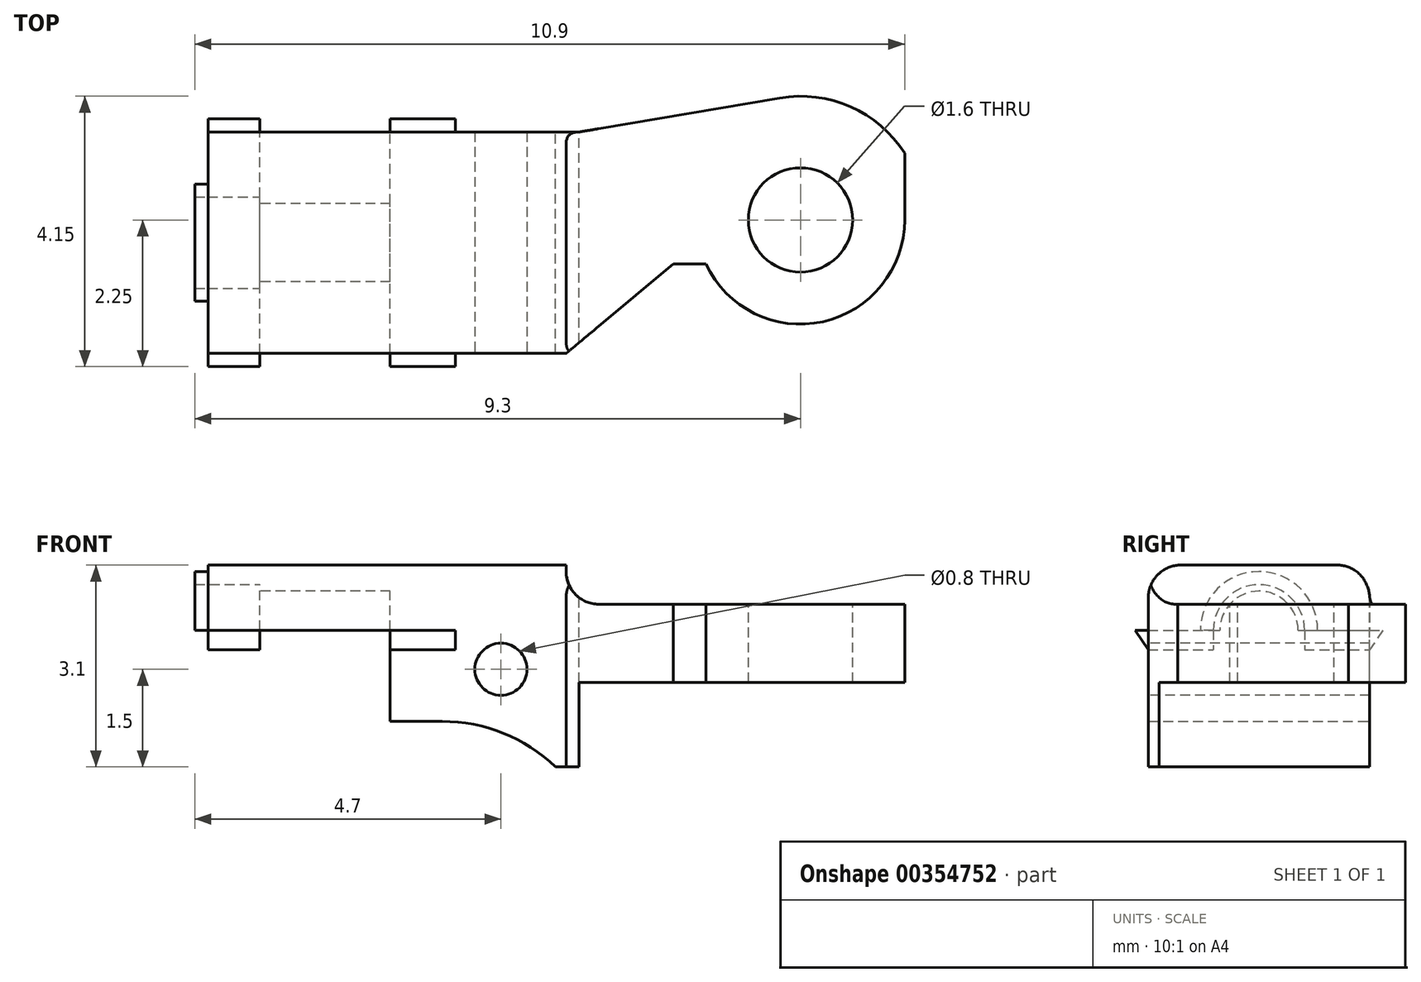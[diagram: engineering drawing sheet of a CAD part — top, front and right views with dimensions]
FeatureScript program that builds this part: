
annotation { "Feature Type Name" : "Feature", "Feature Type Description" : "" }
export const myFeature = defineFeature(function(context is Context, id is Id, definition is map)
    precondition{}
    {
        {
            var Q0;
            Q0=qCreatedBy(makeId("Front.planeOp"),FACE);
            var sketch = newSketch(context, id + "F0", { "sketchPlane" : qUnion([Q0])});
            skLineSegment(sketch, "E0", {"start": v(0, 0) * mm, "end": v(0, 2.4) * mm});
            skLineSegment(sketch, "E1", {"start": v(0, 2.4) * mm, "end": v(4.7, 2.4) * mm});
            skLineSegment(sketch, "E2", {"start": v(4.7, 2.4) * mm, "end": v(4.7, 2.4) * mm});
            skLineSegment(sketch, "E3", {"start": v(4.7, 1.8) * mm, "end": v(4.7, 2.4) * mm});
            skLineSegment(sketch, "E4", {"start": v(4.7, 1.8) * mm, "end": v(9.9, 1.8) * mm});
            skLineSegment(sketch, "E5", {"start": v(9.9, 1.8) * mm, "end": v(9.9, 0.6) * mm});
            skLineSegment(sketch, "E6", {"start": v(9.9, 0.6) * mm, "end": v(4.9, 0.6) * mm});
            skLineSegment(sketch, "E7", {"start": v(4.9, 0.6) * mm, "end": v(4.9, -0.7) * mm});
            skLineSegment(sketch, "E8", {"start": v(2.8, 0) * mm, "end": v(0, 0) * mm});
            skArc(sketch, "E9", {"start": v(4.53, -0.7) * mm, "mid": v(3.74, -0.18) * mm, "end": v(2.8, 0) * mm});
            skLineSegment(sketch, "E10", {"start": v(4.53, -0.7) * mm, "end": v(4.9, -0.7) * mm});
            skPoint(sketch, "E11.orphan", {"position": v(4.9, 0) * mm});
            skSolve(sketch);
        }
        {
            var Q0;
            Q0 = qSketchRegion(id + "F0", true);
            extrude(context, id + "F1", {"entities" : qUnion([Q0]), "endBound" : BoundingType.SYMMETRIC, "depth" : 3.4 * mm});
        }
        {
            var Q0;
            Q0=makeQuery(id+"F1.opExtrude","SWEPT_FACE",FACE,{"disambiguationData":[OSD([sQuery(id+"F0.wireOp",EDGE,"E4")])]});
            var sketch = newSketch(context, id + "F2", { "sketchPlane" : qUnion([Q0])});
            skCircle(sketch, "E12", {"center": v(8.3, 0.35) * mm, "radius": 0.8 * mm});
            skArc(sketch, "E13", {"start": v(9.9, 0.35) * mm, "mid": v(8.65, -1.21) * mm, "end": v(6.85, -0.33) * mm});
            skLineSegment(sketch, "E14", {"start": v(8.3, 0.35) * mm, "end": v(6.85, -0.33) * mm, "construction": true});
            skLineSegment(sketch, "E15", {"start": v(4.7, -1.7) * mm, "end": v(6.35, -0.33) * mm});
            skLineSegment(sketch, "E16", {"start": v(6.35, -0.33) * mm, "end": v(6.85, -0.33) * mm});
            skLineSegment(sketch, "E17", {"start": v(9.9, 1.7) * mm, "end": v(9.9, 1.37) * mm});
            skLineSegment(sketch, "E18", {"start": v(9.9, -1.7) * mm, "end": v(4.7, -1.7) * mm});
            skPoint(sketch, "E19.orphan", {"position": v(6.85, -0.33) * mm});
            skLineSegment(sketch, "E20", {"start": v(9.9, 1.7) * mm, "end": v(9.64, 1.7) * mm});
            skPoint(sketch, "E21.orphan", {"position": v(9.9, 0.35) * mm});
            skArc(sketch, "E22", {"start": v(9.9, 1.37) * mm, "mid": v(9.78, 1.54) * mm, "end": v(9.64, 1.7) * mm});
            skLineSegment(sketch, "E23.trimOffspring", {"start": v(9.9, 0.35) * mm, "end": v(9.9, -1.7) * mm});
            skSolve(sketch);
        }
        {
            var Q0;
            Q0 = qSketchRegion(id + "F2", true);
            extrude(context, id + "F3", {"entities" : qUnion([Q0]), "operationType" : NewBodyOperationType.REMOVE, "endBound" : BoundingType.THROUGH_ALL, "oppositeDirection" : true, "depth" : 25 * mm});
        }
        {
            var Q0;
            Q0=makeQuery(id+"F1.opExtrude","SWEPT_FACE",FACE,{"disambiguationData":[OSD([sQuery(id+"F0.wireOp",EDGE,"E4")])]});
            var sketch = newSketch(context, id + "F4", { "sketchPlane" : qUnion([Q0])});
            skArc(sketch, "E24", {"start": v(9.64, 1.7) * mm, "mid": v(8.87, 2.16) * mm, "end": v(7.98, 2.22) * mm});
            skLineSegment(sketch, "E25", {"start": v(4.9, 1.7) * mm, "end": v(7.98, 2.22) * mm});
            skLineSegment(sketch, "E26", {"start": v(4.9, 1.7) * mm, "end": v(9.64, 1.7) * mm});
            skSolve(sketch);
        }
        {
            var Q0;
            Q0=makeQuery(id+"F4.imprint","IMPRINT",FACE,{"disambiguationData":[TD([[makeQuery(id+"F4.imprint","IMPRINT",EDGE,{"derivedFrom":sQuery(id+"F4.wireOp",EDGE,"E24")}),1.0]])]});
            var Q1;
            Q1=makeQuery(id+"F1.opExtrude","SWEPT_FACE",FACE,{"disambiguationData":[OSD([sQuery(id+"F0.wireOp",EDGE,"E6")])]});
            extrude(context, id + "F5", {"entities" : qUnion([Q0]), "operationType" : NewBodyOperationType.ADD, "endBound" : BoundingType.UP_TO_SURFACE, "oppositeDirection" : true, "endBoundEntityFace" : qUnion([Q1]), "depth" : 25 * mm});
        }
        {
            var Q0;
            Q0=makeQuery(id+"F1.opExtrude","SWEPT_FACE",FACE,{"disambiguationData":[OSD([sQuery(id+"F0.wireOp",EDGE,"E0")])]});
            var sketch = newSketch(context, id + "F6", { "sketchPlane" : qUnion([Q0])});
            skLineSegment(sketch, "E27.bottom", {"start": v(1.7, 0) * mm, "end": v(-1.7, 0) * mm});
            skLineSegment(sketch, "E27.top", {"start": v(1.7, 1.4) * mm, "end": v(0.6, 1.4) * mm});
            skLineSegment(sketch, "E27.left", {"start": v(1.7, 0) * mm, "end": v(1.7, 1.4) * mm});
            skLineSegment(sketch, "E27.right", {"start": v(-1.7, 0) * mm, "end": v(-1.7, 1.4) * mm});
            skArc(sketch, "E28", {"start": v(0.6, 1.4) * mm, "mid": v(0, 2) * mm, "end": v(-0.6, 1.4) * mm});
            skLineSegment(sketch, "E29.trimOffspring", {"start": v(-0.6, 1.4) * mm, "end": v(-1.7, 1.4) * mm});
            skSolve(sketch);
        }
        {
            var Q0;
            Q0 = qSketchRegion(id + "F6", true);
            extrude(context, id + "F7", {"entities" : qUnion([Q0]), "operationType" : NewBodyOperationType.REMOVE, "oppositeDirection" : true, "depth" : 2 * mm});
        }
        {
            var Q0;
            Q0=makeQuery(id+"F1.opExtrude","SWEPT_FACE",FACE,{"disambiguationData":[OSD([sQuery(id+"F0.wireOp",EDGE,"E0")])]});
            var sketch = newSketch(context, id + "F8", { "sketchPlane" : qUnion([Q0])});
            skArc(sketch, "E30", {"start": v(0.7, 1.4) * mm, "mid": v(0, 2.1) * mm, "end": v(-0.7, 1.4) * mm});
            skLineSegment(sketch, "E31", {"start": v(-0.7, 1.1) * mm, "end": v(-1.7, 1.1) * mm});
            skLineSegment(sketch, "E32", {"start": v(1.7, 2.4) * mm, "end": v(1.7, 1.1) * mm});
            skLineSegment(sketch, "E33", {"start": v(1.7, 1.1) * mm, "end": v(0.7, 1.1) * mm});
            skLineSegment(sketch, "E34", {"start": v(0.7, 1.4) * mm, "end": v(0.7, 1.1) * mm});
            skLineSegment(sketch, "E35", {"start": v(-0.7, 1.4) * mm, "end": v(-0.7, 1.1) * mm});
            skLineSegment(sketch, "E36", {"start": v(1.7, 2.4) * mm, "end": v(-1.7, 2.4) * mm});
            skLineSegment(sketch, "E37", {"start": v(-1.7, 2.4) * mm, "end": v(-1.7, 1.1) * mm});
            skSolve(sketch);
        }
        {
            var Q0;
            Q0 = qSketchRegion(id + "F8", true);
            extrude(context, id + "F9", {"entities" : qUnion([Q0]), "operationType" : NewBodyOperationType.ADD, "depth" : 0.8 * mm});
        }
        {
            var Q0;
            Q0=makeQuery(id+"F9.opExtrude","CAP_FACE",FACE,{"disambiguationData":[OSD([sQuery(id+"F8.wireOp",EDGE,"E30"),sQuery(id+"F8.wireOp",EDGE,"33daba41-ab30-421a-8f09-6baf427ecfd6"),sQuery(id+"F8.wireOp",EDGE,"E31"),sQuery(id+"F8.wireOp",EDGE,"E32"),sQuery(id+"F8.wireOp",EDGE,"E33"),sQuery(id+"F8.wireOp",EDGE,"E34"),sQuery(id+"F8.wireOp",EDGE,"E35"),sQuery(id+"F8.wireOp",EDGE,"E36"),sQuery(id+"F8.wireOp",EDGE,"E37"),sQuery(id+"F8.wireOp",EDGE,"b7cedbdc-8d8d-4e8a-a9b7-a7e40b9fc0be.trimOffspring")])],"isStart":false});
            var sketch = newSketch(context, id + "F10", { "sketchPlane" : qUnion([Q0])});
            skArc(sketch, "E38", {"start": v(0.7, 1.4) * mm, "mid": v(0, 2.1) * mm, "end": v(-0.7, 1.4) * mm});
            skArc(sketch, "E39", {"start": v(0.9, 1.4) * mm, "mid": v(0, 2.3) * mm, "end": v(-0.9, 1.4) * mm});
            skLineSegment(sketch, "E40", {"start": v(0.7, 1.4) * mm, "end": v(0.9, 1.4) * mm});
            skLineSegment(sketch, "E41", {"start": v(-0.7, 1.4) * mm, "end": v(-0.9, 1.4) * mm});
            skSolve(sketch);
        }
        {
            var Q0;
            Q0 = qSketchRegion(id + "F10", true);
            extrude(context, id + "F11", {"entities" : qUnion([Q0]), "operationType" : NewBodyOperationType.ADD, "depth" : 0.2 * mm});
        }
        {
            var Q0;
            Q0=makeQuery(id+"F9.boolean.opBoolean","MERGE",FACE,{"derivedFrom":[makeQuery(id+"F1.opExtrude","CAP_FACE",FACE,{"disambiguationData":[OSD([sQuery(id+"F0.wireOp",EDGE,"E0"),sQuery(id+"F0.wireOp",EDGE,"E1"),sQuery(id+"F0.wireOp",EDGE,"E3"),sQuery(id+"F0.wireOp",EDGE,"E4"),sQuery(id+"F0.wireOp",EDGE,"E5"),sQuery(id+"F0.wireOp",EDGE,"E6"),sQuery(id+"F0.wireOp",EDGE,"E7"),sQuery(id+"F0.wireOp",EDGE,"E8"),sQuery(id+"F0.wireOp",EDGE,"E9"),sQuery(id+"F0.wireOp",EDGE,"E10")])],"isStart":false}),makeQuery(id+"F9.opExtrude","SWEPT_FACE",FACE,{"disambiguationData":[OSD([sQuery(id+"F8.wireOp",EDGE,"E32")])]})]});
            var sketch = newSketch(context, id + "F12", { "sketchPlane" : qUnion([Q0])});
            skPoint(sketch, "E42", {"position": v(3.7, 0.8) * mm});
            skCircle(sketch, "E43", {"center": v(3.7, 0.8) * mm, "radius": 0.4 * mm});
            skSolve(sketch);
        }
        {
            var Q0;
            Q0 = qSketchRegion(id + "F12", true);
            extrude(context, id + "F13", {"entities" : qUnion([Q0]), "operationType" : NewBodyOperationType.REMOVE, "endBound" : BoundingType.THROUGH_ALL, "oppositeDirection" : true, "depth" : 25 * mm});
        }
        {
            var Q0;
            Q0=makeQuery(id+"F9.opExtrude","CAP_FACE",FACE,{"disambiguationData":[OSD([sQuery(id+"F8.wireOp",EDGE,"E30"),sQuery(id+"F8.wireOp",EDGE,"E31"),sQuery(id+"F8.wireOp",EDGE,"E32"),sQuery(id+"F8.wireOp",EDGE,"E33"),sQuery(id+"F8.wireOp",EDGE,"E34"),sQuery(id+"F8.wireOp",EDGE,"E35"),sQuery(id+"F8.wireOp",EDGE,"E36"),sQuery(id+"F8.wireOp",EDGE,"E37")])],"isStart":false});
            var sketch = newSketch(context, id + "F14", { "sketchPlane" : qUnion([Q0])});
            skLineSegment(sketch, "E44", {"start": v(1.7, 1.4) * mm, "end": v(1.9, 1.4) * mm});
            skLineSegment(sketch, "E45", {"start": v(1.9, 1.4) * mm, "end": v(1.7, 1.1) * mm});
            skLineSegment(sketch, "E46", {"start": v(1.7, 1.1) * mm, "end": v(1.7, 1.4) * mm});
            skLineSegment(sketch, "E47", {"start": v(-1.7, 1.4) * mm, "end": v(-1.9, 1.4) * mm});
            skLineSegment(sketch, "E48", {"start": v(-1.9, 1.4) * mm, "end": v(-1.7, 1.1) * mm});
            skLineSegment(sketch, "E49", {"start": v(-1.7, 1.1) * mm, "end": v(-1.7, 1.4) * mm});
            skSolve(sketch);
        }
        {
            var Q0;
            Q0 = qSketchRegion(id + "F14", true);
            var Q1;
            {var subQ0=sQuery(id+"F8.wireOp",EDGE,"E30");var subQ2=sQuery(id+"F8.wireOp",EDGE,"E32");var subQ3=sQuery(id+"F8.wireOp",EDGE,"E33");var subQ4=sQuery(id+"F8.wireOp",EDGE,"E34");Q1=makeQuery(id+"F9.boolean.opBoolean","SPLIT",FACE,{"disambiguationData":[TD([makeQuery(id+"F7.boolean.opBoolean","COPY",FACE,{"derivedFrom":makeQuery(id+"F7.opExtrude","SWEPT_FACE",FACE,{"disambiguationData":[OSD([sQuery(id+"F6.wireOp",EDGE,"E27.top")])]})})])],"derivedFrom":makeQuery(id+"F9.opExtrude","CAP_FACE",FACE,{"disambiguationData":[OSD([subQ0,sQuery(id+"F8.wireOp",EDGE,"E31"),subQ2,subQ3,subQ4,sQuery(id+"F8.wireOp",EDGE,"E35"),sQuery(id+"F8.wireOp",EDGE,"E36"),sQuery(id+"F8.wireOp",EDGE,"E37")])],"isStart":true})});}
            extrude(context, id + "F15", {"entities" : qUnion([Q0]), "operationType" : NewBodyOperationType.ADD, "endBound" : BoundingType.UP_TO_SURFACE, "oppositeDirection" : true, "endBoundEntityFace" : qUnion([Q1]), "depth" : 5 * mm});
        }
        {
            var Q0;
            Q0=makeQuery(id+"F7.boolean.opBoolean","COPY",FACE,{"derivedFrom":makeQuery(id+"F7.opExtrude","CAP_FACE",FACE,{"disambiguationData":[OSD([sQuery(id+"F6.wireOp",EDGE,"E27.bottom"),sQuery(id+"F6.wireOp",EDGE,"E27.top"),sQuery(id+"F6.wireOp",EDGE,"E27.left"),sQuery(id+"F6.wireOp",EDGE,"E27.right"),sQuery(id+"F6.wireOp",EDGE,"E28"),sQuery(id+"F6.wireOp",EDGE,"E29.trimOffspring")])],"isStart":false})});
            var sketch = newSketch(context, id + "F16", { "sketchPlane" : qUnion([Q0])});
            skLineSegment(sketch, "E50.0", {"start": v(1.7, 1.4) * mm, "end": v(1.9, 1.4) * mm});
            skLineSegment(sketch, "E51.0", {"start": v(1.9, 1.4) * mm, "end": v(1.7, 1.1) * mm});
            skLineSegment(sketch, "E52.0", {"start": v(-1.7, 1.4) * mm, "end": v(-1.9, 1.4) * mm});
            skLineSegment(sketch, "E53.0", {"start": v(-1.9, 1.4) * mm, "end": v(-1.7, 1.1) * mm});
            skLineSegment(sketch, "E54", {"start": v(-1.7, 1.4) * mm, "end": v(-1.7, 1.1) * mm});
            skLineSegment(sketch, "E55", {"start": v(1.7, 1.4) * mm, "end": v(1.7, 1.1) * mm});
            skSolve(sketch);
        }
        {
            var Q0;
            Q0 = qSketchRegion(id + "F16", true);
            extrude(context, id + "F17", {"entities" : qUnion([Q0]), "operationType" : NewBodyOperationType.ADD, "oppositeDirection" : true, "depth" : 1 * mm});
        }
        {
            var Q0;
            Q0=makeQuery(id+"F9.boolean.opBoolean","MERGE",EDGE,{"derivedFrom":[makeQuery(id+"F1.opExtrude","CAP_EDGE",EDGE,{"disambiguationData":[OSD([sQuery(id+"F0.wireOp",EDGE,"E1")])],"isStart":false}),makeQuery(id+"F9.opExtrude","SWEPT_EDGE",EDGE,{"disambiguationData":[OSD([sQuery(id+"F8.wireOp",EDGE,"E32"),sQuery(id+"F8.wireOp",EDGE,"E36")])]})]});
            var Q1;
            Q1=makeQuery(id+"F9.boolean.opBoolean","MERGE",EDGE,{"derivedFrom":[makeQuery(id+"F1.opExtrude","CAP_EDGE",EDGE,{"disambiguationData":[OSD([sQuery(id+"F0.wireOp",EDGE,"E1")])],"isStart":true}),makeQuery(id+"F9.opExtrude","SWEPT_EDGE",EDGE,{"disambiguationData":[OSD([sQuery(id+"F8.wireOp",EDGE,"E36"),sQuery(id+"F8.wireOp",EDGE,"E37")])]})]});
            fillet(context, id + "F18", {"entities" : qUnion([Q0, Q1]), "radius" : 0.5 * mm, "tangentPropagation" : true, "allowEdgeOverflow" : false});
        }
        {
            var Q0;
            Q0=makeQuery(id+"F1.opExtrude","SWEPT_EDGE",EDGE,{"disambiguationData":[OSD([sQuery(id+"F0.wireOp",EDGE,"E3"),sQuery(id+"F0.wireOp",EDGE,"E4")])]});
            fillet(context, id + "F19", {"entities" : qUnion([Q0]), "radius" : 0.5 * mm, "tangentPropagation" : true, "allowEdgeOverflow" : false});
        }
    });
